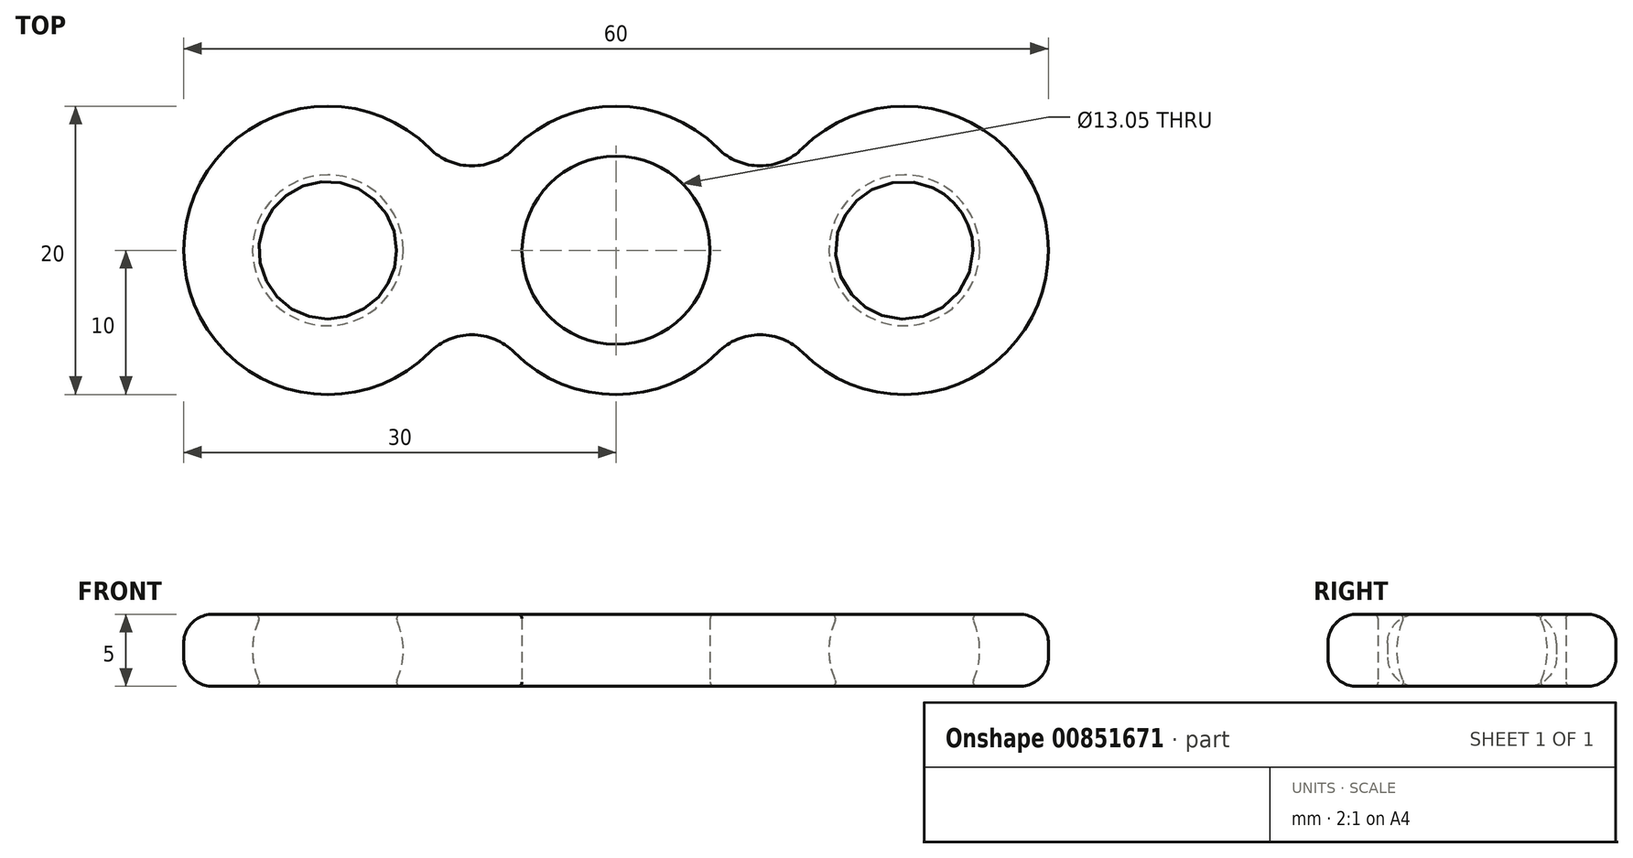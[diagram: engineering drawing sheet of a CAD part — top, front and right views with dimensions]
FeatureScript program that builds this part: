
annotation { "Feature Type Name" : "Feature", "Feature Type Description" : "" }
export const myFeature = defineFeature(function(context is Context, id is Id, definition is map)
    precondition{}
    {
        {
            var Q0;
            Q0=qCreatedBy(makeId("Top.planeOp"),FACE);
            var sketch = newSketch(context, id + "F0", { "sketchPlane" : qUnion([Q0])});
            skArc(sketch, "E0", {"start": v(-7.07, -7.07) * mm, "mid": v(0, -10) * mm, "end": v(7.07, -7.07) * mm});
            skArc(sketch, "E1", {"start": v(12.93, -7.07) * mm, "mid": v(30, 0) * mm, "end": v(12.93, 7.07) * mm});
            skArc(sketch, "E2", {"start": v(-12.93, 7.07) * mm, "mid": v(-30, 0) * mm, "end": v(-12.93, -7.07) * mm});
            skArc(sketch, "E3", {"start": v(7.07, 7.07) * mm, "mid": v(10, 5.86) * mm, "end": v(12.93, 7.07) * mm});
            skArc(sketch, "E4", {"start": v(-12.93, 7.07) * mm, "mid": v(-10, 5.86) * mm, "end": v(-7.07, 7.07) * mm});
            skArc(sketch, "E5.trimOffspring", {"start": v(7.07, 7.07) * mm, "mid": v(0, 10) * mm, "end": v(-7.07, 7.07) * mm});
            skArc(sketch, "E6", {"start": v(-7.07, -7.07) * mm, "mid": v(-10, -5.86) * mm, "end": v(-12.93, -7.07) * mm});
            skArc(sketch, "E7", {"start": v(12.93, -7.07) * mm, "mid": v(10, -5.86) * mm, "end": v(7.07, -7.07) * mm});
            skCircle(sketch, "E8", {"center": v(0, 0) * mm, "radius": 6.53 * mm});
            skSolve(sketch);
        }
        {
            var Q0;
            Q0=makeQuery(id+"F0.imprint","IMPRINT",FACE,{"disambiguationData":[TD([[makeQuery(id+"F0.imprint","IMPRINT",EDGE,{"derivedFrom":sQuery(id+"F0.wireOp",EDGE,"E0")}),1.0]])]});
            extrude(context, id + "F1", {"entities" : qUnion([Q0]), "depth" : 2.5 * mm, "offsetDistance" : 25 * mm});
        }
        {
            var Q0;
            Q0=makeQuery(id+"F1.opExtrude","CAP_FACE",FACE,{"disambiguationData":[OSD([sQuery(id+"F0.wireOp",EDGE,"E0"),sQuery(id+"F0.wireOp",EDGE,"E1"),sQuery(id+"F0.wireOp",EDGE,"E2"),sQuery(id+"F0.wireOp",EDGE,"E3"),sQuery(id+"F0.wireOp",EDGE,"E4"),sQuery(id+"F0.wireOp",EDGE,"E5.trimOffspring"),sQuery(id+"F0.wireOp",EDGE,"E6"),sQuery(id+"F0.wireOp",EDGE,"E7"),sQuery(id+"F0.wireOp",EDGE,"E8")])],"isStart":true});
            extrude(context, id + "F2", {"entities" : qUnion([Q0]), "operationType" : NewBodyOperationType.ADD, "depth" : 2.5 * mm, "offsetDistance" : 25 * mm});
        }
        {
            var Q0;
            Q0=qCreatedBy(makeId("Front.planeOp"),FACE);
            var sketch = newSketch(context, id + "F3", { "sketchPlane" : qUnion([Q0])});
            skArc(sketch, "E9", {"start": v(-20, 5.23) * mm, "mid": v(-25.23, 0) * mm, "end": v(-20, -5.23) * mm});
            skLineSegment(sketch, "E10", {"start": v(-20, 5.23) * mm, "end": v(-20, -5.23) * mm});
            skSolve(sketch);
        }
        {
            var Q0;
            Q0=qSketchRegion(id+"F3",true);
            var Q1;
            Q1=sQuery(id+"F3.wireOp",EDGE,"E10");
            revolve(context, id + "F4", {"operationType" : NewBodyOperationType.REMOVE, "entities" : qUnion([Q0]), "axis" : qUnion([Q1]), "revolveType" : RevolveType.FULL, "oppositeDirection" : true, "surfaceOperationType" : NewSurfaceOperationType.NEW});
        }
        {
            var Q0;
            Q0=qCreatedBy(makeId("Front.planeOp"),FACE);
            var sketch = newSketch(context, id + "F5", { "sketchPlane" : qUnion([Q0])});
            skArc(sketch, "E11", {"start": v(20, -5.23) * mm, "mid": v(25.23, 0) * mm, "end": v(20, 5.23) * mm});
            skLineSegment(sketch, "E12", {"start": v(20, 5.23) * mm, "end": v(20, -5.23) * mm});
            skPoint(sketch, "E13.orphan", {"position": v(20, 9.13) * mm});
            skSolve(sketch);
        }
        {
            var Q0;
            Q0=makeQuery(id+"F5.imprint","IMPRINT",FACE,{"disambiguationData":[TD([[makeQuery(id+"F5.imprint","IMPRINT",EDGE,{"derivedFrom":sQuery(id+"F5.wireOp",EDGE,"E11")}),1.0]])]});
            var Q1;
            Q1=sQuery(id+"F5.wireOp",EDGE,"E12");
            revolve(context, id + "F6", {"operationType" : NewBodyOperationType.REMOVE, "entities" : qUnion([Q0]), "axis" : qUnion([Q1]), "revolveType" : RevolveType.FULL, "oppositeDirection" : true});
        }
        {
            var Q0;
            Q0=makeQuery(id+"F2.opExtrude","CAP_EDGE",EDGE,{"disambiguationData":[OSD([sQuery(id+"F0.wireOp",EDGE,"E6")])],"isStart":false});
            var Q1;
            Q1=makeQuery(id+"F1.opExtrude","CAP_EDGE",EDGE,{"disambiguationData":[OSD([sQuery(id+"F0.wireOp",EDGE,"E0")])],"isStart":false});
            fillet(context, id + "F7", {"entities" : qUnion([Q0, Q1]), "radius" : 2 * mm, "tangentPropagation" : true, "allowEdgeOverflow" : false});
        }
        {
            var Q0;
            Q0=makeQuery(id+"F6.boolean.opBoolean","COPY",FACE,{"derivedFrom":makeQuery(id+"F6.opRevolve","SWEPT_FACE",FACE,{"disambiguationData":[OSD([sQuery(id+"F5.wireOp",EDGE,"E11")])]})});
            var Q1;
            {var subQ0=sQuery(id+"F0.wireOp",EDGE,"E8");Q1=makeQuery(id+"F2.boolean.opBoolean","MERGE",FACE,{"derivedFrom":[makeQuery(id+"F1.opExtrude","SWEPT_FACE",FACE,{"disambiguationData":[OSD([subQ0])]}),makeQuery(id+"F2.opExtrude","SWEPT_FACE",FACE,{"disambiguationData":[OSD([subQ0])]})]});}
            var Q2;
            Q2=makeQuery(id+"F4.boolean.opBoolean","COPY",FACE,{"derivedFrom":makeQuery(id+"F4.opRevolve","SWEPT_FACE",FACE,{"disambiguationData":[OSD([sQuery(id+"F3.wireOp",EDGE,"E9")])]})});
            fillet(context, id + "F8", {"entities" : qUnion([Q0, Q1, Q2]), "radius" : .3 * mm, "tangentPropagation" : true, "allowEdgeOverflow" : false});
        }
    });
